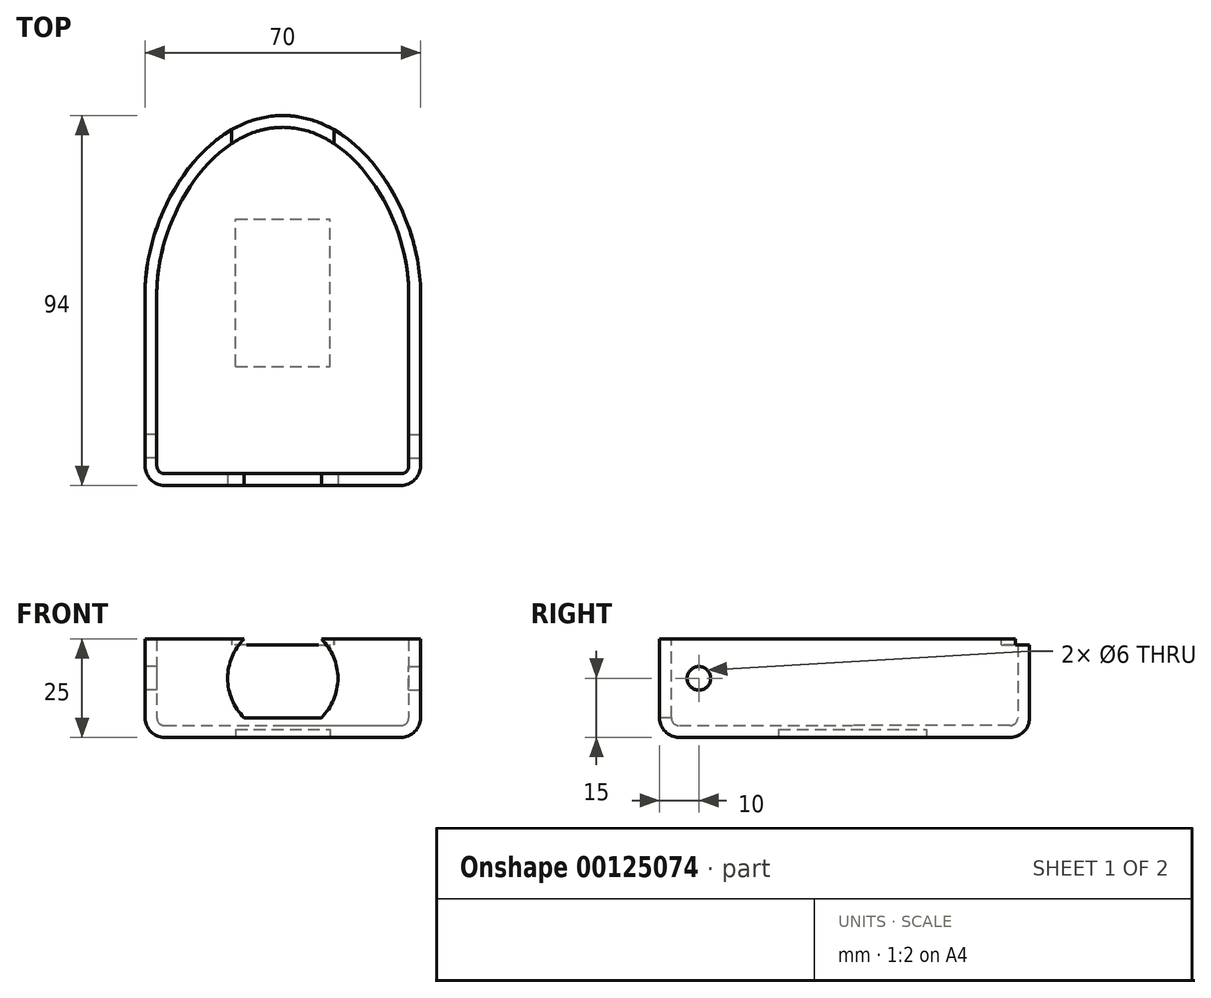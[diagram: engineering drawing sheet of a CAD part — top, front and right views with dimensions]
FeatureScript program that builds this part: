
annotation { "Feature Type Name" : "Feature", "Feature Type Description" : "" }
export const myFeature = defineFeature(function(context is Context, id is Id, definition is map)
    precondition{}
    {
        {
            var Q0;
            Q0=qCreatedBy(makeId("Top.planeOp"),FACE);
            var sketch = newSketch(context, id + "F0", { "sketchPlane" : qUnion([Q0])});
            skLineSegment(sketch, "E0.top", {"start": v(-35, -49) * mm, "end": v(35, -49) * mm});
            skPoint(sketch, "E0.middle", {"position": v(0, 0) * mm});
            skPoint(sketch, "E1.visualSharp", {"position": v(-35, -49) * mm});
            skPoint(sketch, "E2.visualSharp", {"position": v(35, -49) * mm});
            skPoint(sketch, "E3", {"position": v(-35, 0) * mm});
            skPoint(sketch, "E4", {"position": v(35, 0) * mm});
            skLineSegment(sketch, "E5", {"start": v(-35, 0) * mm, "end": v(-35, -49) * mm});
            skLineSegment(sketch, "E6", {"start": v(35, 0) * mm, "end": v(35, -49) * mm});
            skFitSpline(sketch, "E7", {"points": [v(0, 45) * mm, v(-35, 0) * mm], "startDerivative": vector(-60.6, 0) * mm, "endDerivative": vector(0, -60.15) * mm});
            skFitSpline(sketch, "E8.MirrorCS", {"points": [v(0, 45) * mm, v(35, 0) * mm], "startDerivative": vector(60.6, 0) * mm, "endDerivative": vector(0, -60.15) * mm});
            skSolve(sketch);
        }
        {
            var Q0;
            Q0=qSketchRegion(id+"F0",true);
            extrude(context, id + "F1", {"entities" : qUnion([Q0]), "endBound" : BoundingType.SYMMETRIC, "depth" : 30 * mm});
        }
        {
            var Q0;
            Q0=qCreatedBy(makeId("Right.planeOp"),FACE);
            var sketch = newSketch(context, id + "F2", { "sketchPlane" : qUnion([Q0])});
            skLineSegment(sketch, "E9", {"start": v(0, 0) * mm, "end": v(-30, 0) * mm});
            skPoint(sketch, "E10", {"position": v(-30, 0) * mm});
            skLineSegment(sketch, "E11", {"start": v(-30, 12.5) * mm, "end": v(-30, -12.5) * mm});
            skLineSegment(sketch, "E12", {"start": v(-30, -12.5) * mm, "end": v(0, -12.5) * mm});
            skLineSegment(sketch, "E13", {"start": v(-30, 12.5) * mm, "end": v(-15.57, -12.5) * mm});
            skLineSegment(sketch, "E14", {"start": v(-30, 7.5) * mm, "end": v(-27.11, 7.5) * mm});
            skLineSegment(sketch, "E15.bottom", {"start": v(-30, 7.5) * mm, "end": v(-40, 7.5) * mm});
            skLineSegment(sketch, "E15.top", {"start": v(-30, -12.5) * mm, "end": v(-40, -12.5) * mm});
            skLineSegment(sketch, "E15.left", {"start": v(-30, 7.5) * mm, "end": v(-30, -12.5) * mm});
            skLineSegment(sketch, "E15.right", {"start": v(-40, 7.5) * mm, "end": v(-40, -12.5) * mm});
            skSolve(sketch);
        }
        {
            var Q0;
            Q0=makeQuery(id+"F1.opExtrude","CAP_FACE",FACE,{"disambiguationData":[OSD([sQuery(id+"F0.wireOp",EDGE,"E0.top"),sQuery(id+"F0.wireOp",EDGE,"49a04736-c9a8-4021-8eca-e335ee950ef4"),sQuery(id+"F0.wireOp",EDGE,"5cda4a63-8e27-4d9c-be18-28a9360ed2950.MirrorCS"),sQuery(id+"F0.wireOp",EDGE,"E5"),sQuery(id+"F0.wireOp",EDGE,"E6")])],"isStart":true});
            var sketch = newSketch(context, id + "F3", { "sketchPlane" : qUnion([Q0])});
            skLineSegment(sketch, "E16.bottom", {"start": v(35, 49) * mm, "end": v(-25, 49) * mm});
            skLineSegment(sketch, "E16.top", {"start": v(35, 64.57) * mm, "end": v(-25, 64.57) * mm});
            skLineSegment(sketch, "E16.left", {"start": v(35, 49) * mm, "end": v(35, 64.57) * mm});
            skLineSegment(sketch, "E16.right", {"start": v(-25, 49) * mm, "end": v(-25, 64.57) * mm});
            skFitSpline(sketch, "E17", {"points": [v(0, -40) * mm, v(30, 0) * mm], "startDerivative": vector(49.89, 0) * mm, "endDerivative": vector(0, 60.15) * mm});
            skFitSpline(sketch, "E18.MirrorCS", {"points": [v(0, -40) * mm, v(-30, 0) * mm], "startDerivative": vector(-49.89, 0) * mm, "endDerivative": vector(0, 60.15) * mm});
            skFitSpline(sketch, "E19.0", {"points": [v(0, -32) * mm, v(0.64, -32) * mm, v(1.9, -31.9) * mm, v(3.77, -31.49) * mm, v(5.66, -30.78) * mm, v(8.18, -29.45) * mm, v(11.32, -27.03) * mm, v(14.84, -22.99) * mm, v(17.86, -18) * mm, v(20.18, -12.32) * mm, v(21.66, -6.22) * mm, v(22, -2.06) * mm, v(22, 0) * mm]});
            skFitSpline(sketch, "E19.1", {"points": [v(0, -32) * mm, v(-0.64, -32) * mm, v(-1.9, -31.9) * mm, v(-3.77, -31.49) * mm, v(-5.66, -30.78) * mm, v(-8.18, -29.45) * mm, v(-11.32, -27.03) * mm, v(-14.84, -22.99) * mm, v(-17.86, -18) * mm, v(-20.18, -12.32) * mm, v(-21.66, -6.22) * mm, v(-22, -2.06) * mm, v(-22, 0) * mm]});
            skFitSpline(sketch, "E20.0", {"points": [v(0, -27) * mm, v(0.4, -27) * mm, v(1.15, -26.94) * mm, v(2.33, -26.68) * mm, v(3.59, -26.21) * mm, v(4.94, -25.5) * mm, v(6.36, -24.53) * mm, v(8.32, -22.85) * mm, v(10.76, -20.06) * mm, v(13.36, -15.76) * mm, v(15.4, -10.78) * mm, v(16.7, -5.42) * mm, v(17, -1.78) * mm, v(17, 0) * mm]});
            skFitSpline(sketch, "E20.1", {"points": [v(0, -27) * mm, v(-0.4, -27) * mm, v(-1.15, -26.94) * mm, v(-2.33, -26.68) * mm, v(-3.59, -26.21) * mm, v(-4.94, -25.5) * mm, v(-6.36, -24.53) * mm, v(-8.32, -22.85) * mm, v(-10.76, -20.06) * mm, v(-13.36, -15.76) * mm, v(-15.4, -10.78) * mm, v(-16.7, -5.42) * mm, v(-17, -1.78) * mm, v(-17, 0) * mm]});
            skLineSegment(sketch, "E21.bottom", {"start": v(-22, 0) * mm, "end": v(22, 0) * mm});
            skLineSegment(sketch, "E21.top", {"start": v(-22, 10) * mm, "end": v(22, 10) * mm});
            skLineSegment(sketch, "E21.left", {"start": v(-22, 0) * mm, "end": v(-22, 10) * mm});
            skLineSegment(sketch, "E21.right", {"start": v(22, 0) * mm, "end": v(22, 10) * mm});
            skLineSegment(sketch, "E22", {"start": v(-20.56, -10.51) * mm, "end": v(-15.34, -10.51) * mm});
            skLineSegment(sketch, "E23.MirrorCS", {"start": v(20.56, -10.51) * mm, "end": v(15.34, -10.51) * mm});
            skLineSegment(sketch, "E24.top", {"start": v(-22, 5) * mm, "end": v(22, 5) * mm});
            skLineSegment(sketch, "E24.left", {"start": v(-22, 10) * mm, "end": v(-22, 5) * mm});
            skLineSegment(sketch, "E24.right", {"start": v(22, 10) * mm, "end": v(22, 5) * mm});
            skSolve(sketch);
        }
        {
            var Q0;
            Q0=makeQuery(id+"F1.opExtrude","CAP_EDGE",EDGE,{"disambiguationData":[OSD([sQuery(id+"F0.wireOp",EDGE,"E5")])],"isStart":true});
            var Q1;
            Q1=makeQuery(id+"F1.opExtrude","CAP_EDGE",EDGE,{"disambiguationData":[OSD([sQuery(id+"F0.wireOp",EDGE,"E7")])],"isStart":true});
            var Q2;
            Q2=makeQuery(id+"F1.opExtrude","CAP_EDGE",EDGE,{"disambiguationData":[OSD([sQuery(id+"F0.wireOp",EDGE,"E0.top")])],"isStart":false});
            var Q3;
            Q3=makeQuery(id+"F1.opExtrude","CAP_EDGE",EDGE,{"disambiguationData":[OSD([sQuery(id+"F0.wireOp",EDGE,"E5")])],"isStart":false});
            var Q4;
            Q4=makeQuery(id+"F1.opExtrude","SWEPT_EDGE",EDGE,{"disambiguationData":[OSD([sQuery(id+"F0.wireOp",EDGE,"E0.top"),sQuery(id+"F0.wireOp",EDGE,"E5")])]});
            var Q5;
            Q5=makeQuery(id+"F1.opExtrude","SWEPT_EDGE",EDGE,{"disambiguationData":[OSD([sQuery(id+"F0.wireOp",EDGE,"E0.top"),sQuery(id+"F0.wireOp",EDGE,"E6")])]});
            var Q6;
            {var subQ0=sQuery(id+"F0.wireOp",EDGE,"E0.top");var subQ1=sQuery(id+"F0.wireOp",EDGE,"E5");Q6=makeQuery(id+"FKo57LURMALH3DB_1.boolean.opBoolean","SPLIT",EDGE,{"disambiguationData":[TD([makeQuery(id+"F1.opExtrude","SWEPT_FACE",FACE,{"disambiguationData":[OSD([subQ1])]})])],"derivedFrom":makeQuery(id+"F1.opExtrude","CAP_EDGE",EDGE,{"disambiguationData":[OSD([subQ0])],"isStart":true})});}
            var Q7;
            {var subQ0=sQuery(id+"F0.wireOp",EDGE,"E0.top");var subQ1=sQuery(id+"F0.wireOp",EDGE,"E6");Q7=makeQuery(id+"FKo57LURMALH3DB_1.boolean.opBoolean","SPLIT",EDGE,{"disambiguationData":[TD([makeQuery(id+"F1.opExtrude","SWEPT_FACE",FACE,{"disambiguationData":[OSD([subQ1])]})])],"derivedFrom":makeQuery(id+"F1.opExtrude","CAP_EDGE",EDGE,{"disambiguationData":[OSD([subQ0])],"isStart":true})});}
            fillet(context, id + "F4", {"entities" : qUnion([Q0, Q1, Q2, Q3, Q4, Q5, Q6, Q7]), "radius" : 5 * mm, "tangentPropagation" : true, "allowEdgeOverflow" : false});
        }
        {
            var Q0;
            Q0=makeQuery(id+"F1.opExtrude","CAP_FACE",FACE,{"disambiguationData":[OSD([sQuery(id+"F0.wireOp",EDGE,"E0.top"),sQuery(id+"F0.wireOp",EDGE,"E5"),sQuery(id+"F0.wireOp",EDGE,"E6"),sQuery(id+"F0.wireOp",EDGE,"E7"),sQuery(id+"F0.wireOp",EDGE,"E8.MirrorCS")])],"isStart":false});
            var sketch = newSketch(context, id + "F5", { "sketchPlane" : qUnion([Q0])});
            skLineSegment(sketch, "E25.bottom", {"start": v(-45.63, 73.42) * mm, "end": v(45.63, 73.42) * mm});
            skLineSegment(sketch, "E25.top", {"start": v(-45.63, -73.42) * mm, "end": v(45.63, -73.42) * mm});
            skLineSegment(sketch, "E25.left", {"start": v(-45.63, 73.42) * mm, "end": v(-45.63, -73.42) * mm});
            skLineSegment(sketch, "E25.right", {"start": v(45.63, 73.42) * mm, "end": v(45.63, -73.42) * mm});
            skPoint(sketch, "E25.middle", {"position": v(0, 0) * mm});
            skSolve(sketch);
        }
        {
            var Q0;
            Q0=qSketchRegion(id+"F5",true);
            extrude(context, id + "F6", {"entities" : qUnion([Q0]), "operationType" : NewBodyOperationType.REMOVE, "oppositeDirection" : true, "depth" : 5 * mm});
        }
        {
            var Q0;
            Q0=makeQuery(id+"F6.boolean.opBoolean","COPY",FACE,{"derivedFrom":makeQuery(id+"F6.opExtrude","CAP_FACE",FACE,{"disambiguationData":[OSD([sQuery(id+"F5.wireOp",EDGE,"E25.bottom"),sQuery(id+"F5.wireOp",EDGE,"E25.top"),sQuery(id+"F5.wireOp",EDGE,"E25.left"),sQuery(id+"F5.wireOp",EDGE,"E25.right")])],"isStart":false})});
            shell(context, id + "F7", {"entities" : qUnion([Q0]), "thickness" : 3 * mm});
        }
        {
            var Q0;
            Q0=makeQuery(id+"F1.opExtrude","SWEPT_FACE",FACE,{"disambiguationData":[OSD([sQuery(id+"F0.wireOp",EDGE,"E0.top")])]});
            var sketch = newSketch(context, id + "F8", { "sketchPlane" : qUnion([Q0])});
            skLineSegment(sketch, "E26.bottom", {"start": v(-30, 10) * mm, "end": v(30, 10) * mm});
            skLineSegment(sketch, "E26.top", {"start": v(-30, -10) * mm, "end": v(30, -10) * mm});
            skLineSegment(sketch, "E26.left", {"start": v(-30, 10) * mm, "end": v(-30, -10) * mm});
            skLineSegment(sketch, "E26.right", {"start": v(30, 10) * mm, "end": v(30, -10) * mm});
            skPoint(sketch, "E27", {"position": v(0, 0) * mm});
            skPoint(sketch, "E28", {"position": v(-17.5, 0) * mm});
            skPoint(sketch, "E29", {"position": v(17.5, 0) * mm});
            skArc(sketch, "E30", {"start": v(-9.8, 10) * mm, "mid": v(-14, 0) * mm, "end": v(-9.8, -10) * mm});
            skLineSegment(sketch, "E31", {"start": v(0, 0) * mm, "end": v(0, 10) * mm});
            skLineSegment(sketch, "E32", {"start": v(0, 0) * mm, "end": v(0, -10) * mm});
            skPoint(sketch, "E32.endSnap0", {"position": v(0, -10) * mm});
            skLineSegment(sketch, "E33", {"start": v(-9.8, 10) * mm, "end": v(9.8, 10) * mm});
            skLineSegment(sketch, "E34", {"start": v(-9.8, -10) * mm, "end": v(9.8, -10) * mm});
            skArc(sketch, "E35.trimOffspring", {"start": v(9.8, -10) * mm, "mid": v(14, 0) * mm, "end": v(9.8, 10) * mm});
            skPoint(sketch, "E36.orphan", {"position": v(0, -14) * mm});
            skSolve(sketch);
        }
        {
            var Q0;
            Q0=makeQuery(id+"F1.opExtrude","CAP_FACE",FACE,{"disambiguationData":[OSD([sQuery(id+"F0.wireOp",EDGE,"E0.top"),sQuery(id+"F0.wireOp",EDGE,"E5"),sQuery(id+"F0.wireOp",EDGE,"E6"),sQuery(id+"F0.wireOp",EDGE,"E7"),sQuery(id+"F0.wireOp",EDGE,"E8.MirrorCS")])],"isStart":true});
            var sketch = newSketch(context, id + "F9", { "sketchPlane" : qUnion([Q0])});
            skLineSegment(sketch, "E37.bottom", {"start": v(-12, 18.75) * mm, "end": v(12, 18.75) * mm});
            skLineSegment(sketch, "E37.top", {"start": v(-12, -18.75) * mm, "end": v(12, -18.75) * mm});
            skLineSegment(sketch, "E37.left", {"start": v(-12, 18.75) * mm, "end": v(-12, -18.75) * mm});
            skLineSegment(sketch, "E37.right", {"start": v(12, 18.75) * mm, "end": v(12, -18.75) * mm});
            skPoint(sketch, "E38", {"position": v(0, 0) * mm});
            skPoint(sketch, "E38.positionSnap0", {"position": v(0, 18.75) * mm});
            skPoint(sketch, "E38.positionSnap1", {"position": v(-12, 0) * mm});
            skSolve(sketch);
        }
        {
            var Q0;
            Q0 = qSketchRegion(id + "F9", true);
            extrude(context, id + "F10", {"entities" : qUnion([Q0]), "operationType" : NewBodyOperationType.REMOVE, "oppositeDirection" : true, "depth" : 2 * mm});
        }
        {
            var Q0;
            {var subQ2=sQuery(id+"F8.wireOp",EDGE,"E31");Q0=makeQuery(id+"F8.imprint","IMPRINT",FACE,{"disambiguationData":[TD([[makeQuery(id+"F8.imprint","IMPRINT",EDGE,{"derivedFrom":subQ2}),-1.0]])]});}
            var Q1;
            {var subQ2=sQuery(id+"F8.wireOp",EDGE,"E30");Q1=makeQuery(id+"F8.imprint","IMPRINT",FACE,{"disambiguationData":[TD([[makeQuery(id+"F8.imprint","IMPRINT",EDGE,{"derivedFrom":subQ2}),1.0]])]});}
            extrude(context, id + "F11", {"entities" : qUnion([Q0, Q1]), "operationType" : NewBodyOperationType.REMOVE, "oppositeDirection" : true, "depth" : 3 * mm});
        }
        {
            var Q0;
            Q0=makeQuery(id+"F6.boolean.opBoolean","COPY",FACE,{"derivedFrom":makeQuery(id+"F6.opExtrude","CAP_FACE",FACE,{"disambiguationData":[OSD([sQuery(id+"F5.wireOp",EDGE,"E25.bottom"),sQuery(id+"F5.wireOp",EDGE,"E25.top"),sQuery(id+"F5.wireOp",EDGE,"E25.left"),sQuery(id+"F5.wireOp",EDGE,"E25.right")])],"isStart":false})});
            var sketch = newSketch(context, id + "F12", { "sketchPlane" : qUnion([Q0])});
            skLineSegment(sketch, "E39.bottom", {"start": v(-13, 37.86) * mm, "end": v(0, 37.86) * mm});
            skLineSegment(sketch, "E39.top", {"start": v(-13, 45) * mm, "end": v(0, 45) * mm});
            skLineSegment(sketch, "E39.left", {"start": v(-13, 37.86) * mm, "end": v(-13, 45) * mm});
            skLineSegment(sketch, "E39.right", {"start": v(0, 37.86) * mm, "end": v(0, 45) * mm});
            skLineSegment(sketch, "E40.bottom", {"start": v(0, 45) * mm, "end": v(13, 45) * mm});
            skLineSegment(sketch, "E40.top", {"start": v(0, 37.86) * mm, "end": v(13, 37.86) * mm});
            skLineSegment(sketch, "E40.left", {"start": v(0, 45) * mm, "end": v(0, 37.86) * mm});
            skLineSegment(sketch, "E40.right", {"start": v(13, 45) * mm, "end": v(13, 37.86) * mm});
            skSolve(sketch);
        }
        {
            var Q0;
            Q0 = qSketchRegion(id + "F12", true);
            extrude(context, id + "F13", {"entities" : qUnion([Q0]), "operationType" : NewBodyOperationType.REMOVE, "oppositeDirection" : true, "depth" : 1.5 * mm});
        }
        {
            var Q0;
            Q0=makeQuery(id+"F1.opExtrude","SWEPT_FACE",FACE,{"disambiguationData":[OSD([sQuery(id+"F0.wireOp",EDGE,"E5")])]});
            var sketch = newSketch(context, id + "F14", { "sketchPlane" : qUnion([Q0])});
            skCircle(sketch, "E41", {"center": v(39, 0) * mm, "radius": 3 * mm});
            skSolve(sketch);
        }
        {
            var Q0;
            Q0=makeQuery(id+"F1.opExtrude","SWEPT_FACE",FACE,{"disambiguationData":[OSD([sQuery(id+"F0.wireOp",EDGE,"E6")])]});
            var sketch = newSketch(context, id + "F15", { "sketchPlane" : qUnion([Q0])});
            skCircle(sketch, "E42", {"center": v(-39, 0) * mm, "radius": 3 * mm});
            skSolve(sketch);
        }
        {
            var Q0;
            Q0 = qSketchRegion(id + "F14", true);
            extrude(context, id + "F16", {"entities" : qUnion([Q0]), "operationType" : NewBodyOperationType.REMOVE, "oppositeDirection" : true, "depth" : 3 * mm});
        }
        {
            var Q0;
            Q0=makeQuery(id+"F15.imprint","IMPRINT",FACE,{"disambiguationData":[TD([[makeQuery(id+"F15.imprint","IMPRINT",EDGE,{"derivedFrom":sQuery(id+"F15.wireOp",EDGE,"E42")}),1.0]])]});
            extrude(context, id + "F17", {"entities" : qUnion([Q0]), "operationType" : NewBodyOperationType.REMOVE, "oppositeDirection" : true, "depth" : 3 * mm});
        }
    });
